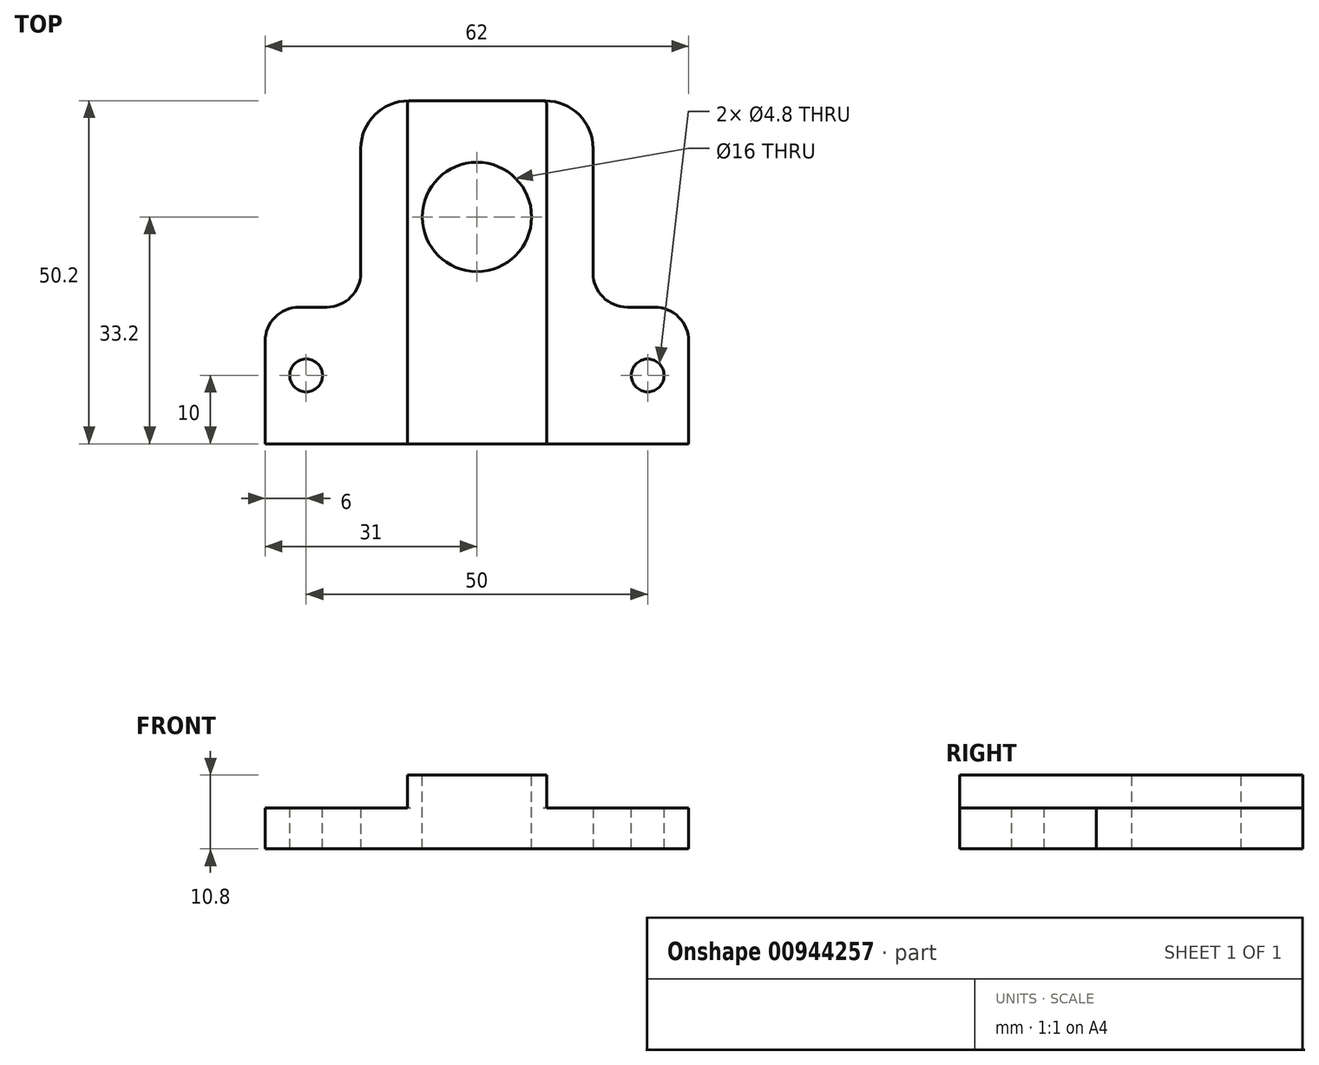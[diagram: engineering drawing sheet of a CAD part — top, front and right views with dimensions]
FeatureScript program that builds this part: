
annotation { "Feature Type Name" : "Feature", "Feature Type Description" : "" }
export const myFeature = defineFeature(function(context is Context, id is Id, definition is map)
    precondition{}
    {
        {
            var Q0;
            Q0=qCreatedBy(makeId("Top.planeOp"),FACE);
            var sketch = newSketch(context, id + "F0", { "sketchPlane" : qUnion([Q0])});
            skLineSegment(sketch, "E0.bottom", {"start": v(-31, 0) * mm, "end": v(31, 0) * mm});
            skLineSegment(sketch, "E0.top", {"start": v(-31, 20) * mm, "end": v(-17, 20) * mm});
            skLineSegment(sketch, "E0.left", {"start": v(-31, 0) * mm, "end": v(-31, 20) * mm});
            skLineSegment(sketch, "E0.right", {"start": v(31, 0) * mm, "end": v(31, 20) * mm});
            skLineSegment(sketch, "E1.top", {"start": v(-17, 50.2) * mm, "end": v(17, 50.2) * mm});
            skLineSegment(sketch, "E1.left", {"start": v(-17, 20) * mm, "end": v(-17, 50.2) * mm});
            skLineSegment(sketch, "E1.right", {"start": v(17, 20) * mm, "end": v(17, 50.2) * mm});
            skLineSegment(sketch, "E2.trimOffspring", {"start": v(17, 20) * mm, "end": v(31, 20) * mm});
            skPoint(sketch, "E3", {"position": v(0, 50.2) * mm});
            skPoint(sketch, "E4", {"position": v(0, 0) * mm});
            skSolve(sketch);
        }
        {
            var Q0;
            Q0=qSketchRegion(id+"F0",true);
            extrude(context, id + "F1", {"entities" : qUnion([Q0]), "depth" : 6 * mm, "offsetDistance" : 25 * mm});
        }
        {
            var Q0;
            Q0=makeQuery(id+"F1.opExtrude","CAP_FACE",FACE,{"disambiguationData":[OSD([sQuery(id+"F0.wireOp",EDGE,"E0.bottom"),sQuery(id+"F0.wireOp",EDGE,"E0.top"),sQuery(id+"F0.wireOp",EDGE,"E0.left"),sQuery(id+"F0.wireOp",EDGE,"E0.right"),sQuery(id+"F0.wireOp",EDGE,"E1.top"),sQuery(id+"F0.wireOp",EDGE,"E1.left"),sQuery(id+"F0.wireOp",EDGE,"E1.right"),sQuery(id+"F0.wireOp",EDGE,"E2.trimOffspring")])],"isStart":false});
            var sketch = newSketch(context, id + "F2", { "sketchPlane" : qUnion([Q0])});
            skLineSegment(sketch, "E5.bottom", {"start": v(-10.2, 50.2) * mm, "end": v(10.2, 50.2) * mm});
            skLineSegment(sketch, "E5.top", {"start": v(-10.2, 0) * mm, "end": v(10.2, 0) * mm});
            skLineSegment(sketch, "E5.left", {"start": v(-10.2, 50.2) * mm, "end": v(-10.2, 0) * mm});
            skLineSegment(sketch, "E5.right", {"start": v(10.2, 50.2) * mm, "end": v(10.2, 0) * mm});
            skPoint(sketch, "E6", {"position": v(0, 50.2) * mm});
            skSolve(sketch);
        }
        {
            var Q0;
            Q0=qSketchRegion(id+"F2",true);
            extrude(context, id + "F3", {"entities" : qUnion([Q0]), "operationType" : NewBodyOperationType.ADD, "depth" : 4.8 * mm, "offsetDistance" : 25 * mm});
        }
        {
            var Q0;
            Q0=makeQuery(id+"F3.opExtrude","CAP_FACE",FACE,{"disambiguationData":[OSD([sQuery(id+"F2.wireOp",EDGE,"E5.bottom"),sQuery(id+"F2.wireOp",EDGE,"E5.top"),sQuery(id+"F2.wireOp",EDGE,"E5.left"),sQuery(id+"F2.wireOp",EDGE,"E5.right")])],"isStart":false});
            var sketch = newSketch(context, id + "F4", { "sketchPlane" : qUnion([Q0])});
            skCircle(sketch, "E7", {"center": v(0, 33.2) * mm, "radius": 8 * mm});
            skSolve(sketch);
        }
        {
            var Q0;
            Q0=qSketchRegion(id+"F4",true);
            extrude(context, id + "F5", {"entities" : qUnion([Q0]), "operationType" : NewBodyOperationType.REMOVE, "endBound" : BoundingType.THROUGH_ALL, "oppositeDirection" : true, "depth" : 25 * mm, "offsetDistance" : 25 * mm});
        }
        {
            var Q0;
            {var subQ0=sQuery(id+"F0.wireOp",EDGE,"E1.top");var subQ1=sQuery(id+"F0.wireOp",EDGE,"E0.left");var subQ2=sQuery(id+"F0.wireOp",EDGE,"E0.top");var subQ3=sQuery(id+"F0.wireOp",EDGE,"E0.bottom");var subQ4=sQuery(id+"F0.wireOp",EDGE,"E1.left");Q0=makeQuery(id+"F3.boolean.opBoolean","SPLIT",FACE,{"disambiguationData":[TD([makeQuery(id+"F1.opExtrude","SWEPT_FACE",FACE,{"disambiguationData":[OSD([subQ2])]})])],"derivedFrom":makeQuery(id+"F1.opExtrude","CAP_FACE",FACE,{"disambiguationData":[OSD([subQ3,subQ2,subQ1,sQuery(id+"F0.wireOp",EDGE,"E0.right"),subQ0,subQ4,sQuery(id+"F0.wireOp",EDGE,"E1.right"),sQuery(id+"F0.wireOp",EDGE,"E2.trimOffspring")])],"isStart":false})});}
            var sketch = newSketch(context, id + "F6", { "sketchPlane" : qUnion([Q0])});
            skCircle(sketch, "E8", {"center": v(-25, 10) * mm, "radius": 2.4 * mm});
            skCircle(sketch, "E9.MirrorC", {"center": v(25, 10) * mm, "radius": 2.4 * mm});
            skSolve(sketch);
        }
        {
            var Q0;
            Q0=qSketchRegion(id+"F6",true);
            extrude(context, id + "F7", {"entities" : qUnion([Q0]), "operationType" : NewBodyOperationType.REMOVE, "endBound" : BoundingType.THROUGH_ALL, "oppositeDirection" : true, "depth" : 25 * mm, "offsetDistance" : 25 * mm});
        }
        {
            var Q0;
            Q0=makeQuery(id+"F1.opExtrude","SWEPT_EDGE",EDGE,{"disambiguationData":[OSD([sQuery(id+"F0.wireOp",EDGE,"E1.top"),sQuery(id+"F0.wireOp",EDGE,"E1.right")])]});
            var Q1;
            Q1=makeQuery(id+"F1.opExtrude","SWEPT_EDGE",EDGE,{"disambiguationData":[OSD([sQuery(id+"F0.wireOp",EDGE,"E1.top"),sQuery(id+"F0.wireOp",EDGE,"E1.left")])]});
            fillet(context, id + "F8", {"entities" : qUnion([Q0, Q1]), "radius" : 7 * mm, "tangentPropagation" : true, "allowEdgeOverflow" : false});
        }
        {
            var Q0;
            Q0=makeQuery(id+"F1.opExtrude","SWEPT_EDGE",EDGE,{"disambiguationData":[OSD([sQuery(id+"F0.wireOp",EDGE,"E0.top"),sQuery(id+"F0.wireOp",EDGE,"E0.left")])]});
            var Q1;
            Q1=makeQuery(id+"F1.opExtrude","SWEPT_EDGE",EDGE,{"disambiguationData":[OSD([sQuery(id+"F0.wireOp",EDGE,"E0.right"),sQuery(id+"F0.wireOp",EDGE,"E2.trimOffspring")])]});
            var Q2;
            Q2=makeQuery(id+"F1.opExtrude","SWEPT_EDGE",EDGE,{"disambiguationData":[OSD([sQuery(id+"F0.wireOp",EDGE,"E1.right"),sQuery(id+"F0.wireOp",EDGE,"E2.trimOffspring")])]});
            var Q3;
            Q3=makeQuery(id+"F1.opExtrude","SWEPT_EDGE",EDGE,{"disambiguationData":[OSD([sQuery(id+"F0.wireOp",EDGE,"E0.top"),sQuery(id+"F0.wireOp",EDGE,"E1.left")])]});
            fillet(context, id + "F9", {"entities" : qUnion([Q0, Q1, Q2, Q3]), "radius" : 5 * mm, "tangentPropagation" : true, "allowEdgeOverflow" : false});
        }
        {
            var Q0;
            Q0=makeQuery(id+"F8.opFillet","BLEND_EDGE",EDGE,{"blendedFrom":[makeQuery(id+"F1.opExtrude","SWEPT_EDGE",EDGE,{"disambiguationData":[OSD([sQuery(id+"F0.wireOp",EDGE,"E1.top"),sQuery(id+"F0.wireOp",EDGE,"E1.right")])]}),makeQuery(id+"F3.opExtrude","SWEPT_FACE",FACE,{"disambiguationData":[OSD([sQuery(id+"F2.wireOp",EDGE,"E5.right")])]})],"blendedInto":[makeQuery(id+"F3.opExtrude","SWEPT_FACE",FACE,{"disambiguationData":[OSD([sQuery(id+"F2.wireOp",EDGE,"E5.right")])]})]});
            var Q1;
            Q1=makeQuery(id+"F8.opFillet","BLEND_EDGE",EDGE,{"blendedFrom":[makeQuery(id+"F1.opExtrude","SWEPT_EDGE",EDGE,{"disambiguationData":[OSD([sQuery(id+"F0.wireOp",EDGE,"E1.top"),sQuery(id+"F0.wireOp",EDGE,"E1.left")])]}),makeQuery(id+"F3.opExtrude","SWEPT_FACE",FACE,{"disambiguationData":[OSD([sQuery(id+"F2.wireOp",EDGE,"E5.left")])]})],"blendedInto":[makeQuery(id+"F3.opExtrude","SWEPT_FACE",FACE,{"disambiguationData":[OSD([sQuery(id+"F2.wireOp",EDGE,"E5.left")])]})]});
            fillet(context, id + "F10", {"entities" : qUnion([Q0, Q1]), "radius" : .5 * mm, "tangentPropagation" : true, "allowEdgeOverflow" : false});
        }
    });
